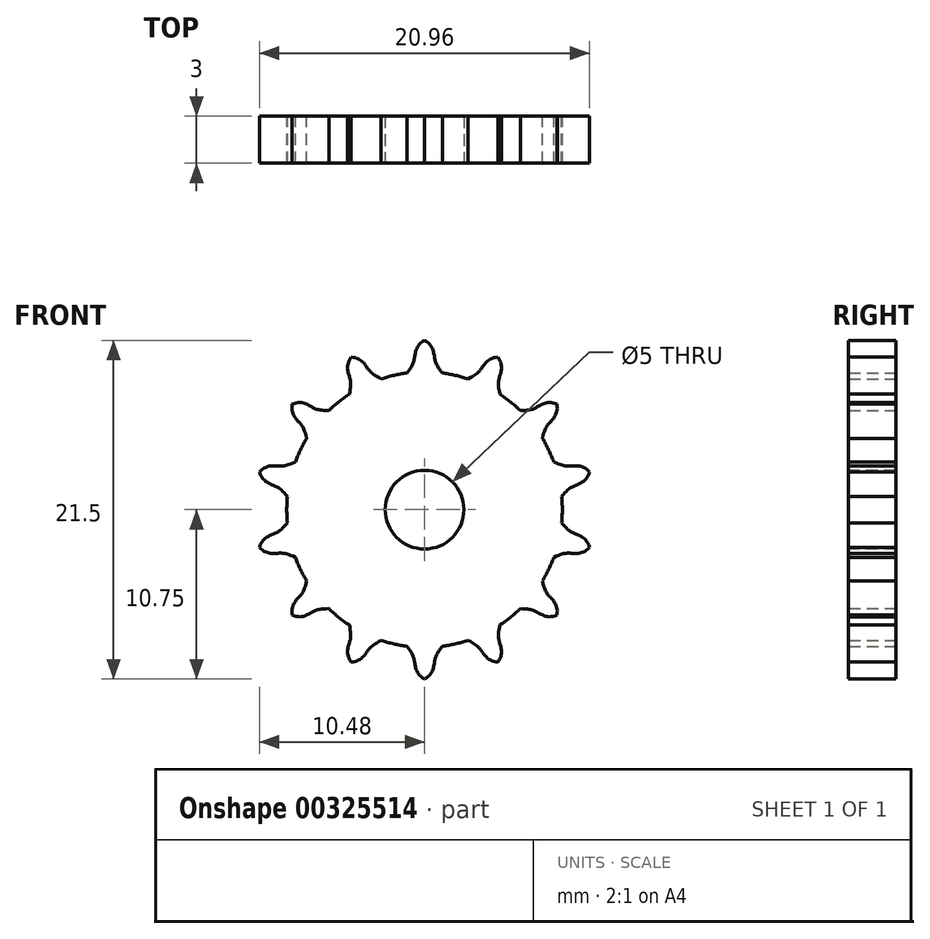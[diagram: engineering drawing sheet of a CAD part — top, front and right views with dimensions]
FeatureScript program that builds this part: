
annotation { "Feature Type Name" : "Feature", "Feature Type Description" : "" }
export const myFeature = defineFeature(function(context is Context, id is Id, definition is map)
    precondition{}
    {
        {
            var Q0;
            Q0=qCreatedBy(makeId("Front.planeOp"),FACE);
            var sketch = newSketch(context, id + "F0", { "sketchPlane" : qUnion([Q0])});
            skCircle(sketch, "E0", {"center": v(0, 0) * mm, "radius": 8.75 * mm, "construction": true});
            skCircle(sketch, "E1", {"center": v(0, 0) * mm, "radius": 10.75 * mm, "construction": true});
            skLineSegment(sketch, "E2", {"start": v(0, 10.75) * mm, "end": v(0, 8.75) * mm, "construction": true});
            skPoint(sketch, "E3", {"position": v(-1.13, 8.68) * mm});
            skPoint(sketch, "E4", {"position": v(1.13, 8.68) * mm});
            skFitSpline(sketch, "E5", {"points": [v(-1.13, 8.68) * mm, v(-0.62, 9.73) * mm, v(0, 10.75) * mm], "startDerivative": vector(2.57, 3.3) * mm, "endDerivative": vector(2.98, 1.56) * mm});
            skFitSpline(sketch, "E6.MirrorCS", {"points": [v(1.13, 8.68) * mm, v(0.62, 9.73) * mm, v(0, 10.75) * mm], "startDerivative": vector(-2.57, 3.3) * mm, "endDerivative": vector(-2.98, 1.56) * mm});
            skArc(sketch, "E7", {"start": v(-1.13, 8.68) * mm, "mid": v(0, -8.75) * mm, "end": v(1.13, 8.68) * mm});
            skCircle(sketch, "E8", {"center": v(0, 0) * mm, "radius": 8.91 * mm, "construction": true});
            skSolve(sketch);
        }
        {
            var Q0;
            Q0 = qSketchRegion(id + "F0", true);
            extrude(context, id + "F1", {"entities" : qUnion([Q0]), "depth" : 3 * mm});
        }
        {
            var Q0;
            Q0=qCreatedBy(makeId("Right.planeOp"),FACE);
            var sketch = newSketch(context, id + "F2", { "sketchPlane" : qUnion([Q0])});
            skLineSegment(sketch, "E9", {"start": v(-21.19, 0) * mm, "end": v(26.28, 0) * mm, "construction": true});
            skSolve(sketch);
        }
        {
            var Q0;
            Q0=makeQuery(id+"F1.opExtrude","SWEPT_BODY",BODY,{"disambiguationData":[OSD([sQuery(id+"F0.wireOp",EDGE,"E5"),sQuery(id+"F0.wireOp",EDGE,"E6.MirrorCS"),sQuery(id+"F0.wireOp",EDGE,"E7")])]});
            var Q1;
            Q1=sQuery(id+"F2.wireOp",EDGE,"E9");
            circularPattern(context, id + "F3", {"operationType" : NewBodyOperationType.ADD, "entities" : qUnion([Q0]), "axis" : qUnion([Q1]), "angle" : 360 * degree, "instanceCount" : 14, "equalSpace" : true});
        }
        {
            var Q0;
            {var subQ0=makeQuery(id+"F1.opExtrude","CAP_FACE",FACE,{"disambiguationData":[OSD([sQuery(id+"F0.wireOp",EDGE,"E5"),sQuery(id+"F0.wireOp",EDGE,"E6.MirrorCS"),sQuery(id+"F0.wireOp",EDGE,"E7")])],"isStart":false});Q0=makeQuery(id+"F3.boolean.opBoolean","MERGE",FACE,{"derivedFrom":[subQ0,makeQuery(id+"F3.opPattern","COPY",FACE,{"derivedFrom":subQ0,"instanceName":"1"}),makeQuery(id+"F3.opPattern","COPY",FACE,{"derivedFrom":subQ0,"instanceName":"2"}),makeQuery(id+"F3.opPattern","COPY",FACE,{"derivedFrom":subQ0,"instanceName":"3"}),makeQuery(id+"F3.opPattern","COPY",FACE,{"derivedFrom":subQ0,"instanceName":"4"}),makeQuery(id+"F3.opPattern","COPY",FACE,{"derivedFrom":subQ0,"instanceName":"5"}),makeQuery(id+"F3.opPattern","COPY",FACE,{"derivedFrom":subQ0,"instanceName":"6"}),makeQuery(id+"F3.opPattern","COPY",FACE,{"derivedFrom":subQ0,"instanceName":"7"}),makeQuery(id+"F3.opPattern","COPY",FACE,{"derivedFrom":subQ0,"instanceName":"8"}),makeQuery(id+"F3.opPattern","COPY",FACE,{"derivedFrom":subQ0,"instanceName":"9"}),makeQuery(id+"F3.opPattern","COPY",FACE,{"derivedFrom":subQ0,"instanceName":"10"}),makeQuery(id+"F3.opPattern","COPY",FACE,{"derivedFrom":subQ0,"instanceName":"11"}),makeQuery(id+"F3.opPattern","COPY",FACE,{"derivedFrom":subQ0,"instanceName":"12"}),makeQuery(id+"F3.opPattern","COPY",FACE,{"derivedFrom":subQ0,"instanceName":"13"}),makeQuery(id+"F3.opPattern","COPY",FACE,{"derivedFrom":subQ0,"instanceName":"14"})]});}
            var sketch = newSketch(context, id + "F4", { "sketchPlane" : qUnion([Q0])});
            skCircle(sketch, "E10", {"center": v(0, 0) * mm, "radius": 2.5 * mm});
            skSolve(sketch);
        }
        {
            var Q0;
            Q0 = qSketchRegion(id + "F4", true);
            extrude(context, id + "F5", {"entities" : qUnion([Q0]), "operationType" : NewBodyOperationType.REMOVE, "endBound" : BoundingType.UP_TO_NEXT, "oppositeDirection" : true, "depth" : 25 * mm});
        }
    });
